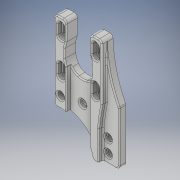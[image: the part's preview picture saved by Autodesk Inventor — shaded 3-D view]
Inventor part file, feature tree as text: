
AUTODESK INVENTOR PART (.ipt)
format: ipt  version: 2018 (Build 220112000, 112)  size: 545,792 bytes
history: native  units: in
note: dims shown in document units (in); Inventor stores cm internally (conversion verified against a paired STEP export)
features: extrude x12, sketch x12, projected_geometry x4, fillet x3, plane x2, chamfer x1
ambient origin geometry x8: Origin, YZ Plane, XZ Plane, XY Plane, X Axis, Y Axis, Z Axis, Center Point
bodies: Solid1 (feature_tree)
feature tree (34):
  extrude  "Extrusion1"  Depth=1.6929in
  extrude  "Extrusion2"  Depth=0.4331in
  fillet  "Fillet1"  Radius=1.6535in
  extrude  "Extrusion3"  Depth=1.2205in
  extrude  "Extrusion4"  Depth=0.126in
  extrude  "Extrusion5"  Depth=0.315in
  extrude  "Extrusion6"  Depth=0.2362in TaperAngle=0.0deg
  plane  "Work Plane1"
  plane  "Work Plane2"
  extrude  "Extrusion7"  Depth=0.1575in TaperAngle=0.0deg
  extrude  "Extrusion8"  Depth=0.2362in
  extrude  "Extrusion9"  Depth=0.9449in
  extrude  "Extrusion10"  Depth=0.6102in
  extrude  "Extrusion11"  Depth=1.2992in
  extrude  "Extrusion12"  Depth=0.1181in
  fillet  "Fillet2"  Radius=7.0866in
  fillet  "Fillet4"  Radius=0.2362in
  chamfer  "Chamfer1"  Distance=0.1654in
  sketch  "Sketch1"  dims[d0=3.8189in d1=1.6929in]
  sketch  "Sketch2"  dims[d2=0.4331in d3=0.4331in d4=1.6535in]
  sketch  "Sketch3"  dims[d5=0.2362in d6=0.0in d7=1.2205in]
  projected_geometry  "Projected Loop1"
  sketch  "Sketch4"  dims[d8=1.2205in d9=0.126in]
  projected_geometry  "Projected Loop2"
  sketch  "Sketch5"  dims[d10=0.2756in d11=0.315in]
  projected_geometry  "Projected Loop3"
  sketch  "Sketch6"  dims[d12=0.315in d13=0.2362in d14=0.0in]
  sketch  "Sketch8"  dims[d15=0.315in d16=0.1575in d17=0.0in]
  sketch  "Sketch9"  dims[d18=0.2362in d20=0.2362in]
  sketch  "Sketch10"  dims[d21=0.1575in d22=0.0in d23=0.9449in]
  projected_geometry  "Projected Loop4"
  sketch  "Sketch11"  dims[d24=0.315in d25=0.6102in]
  sketch  "Sketch12"  dims[d26=0.0in d27=0.0in d28=1.2992in]
  sketch  "Sketch13"  dims[d30=0.2362in d31=0.0in d32=0.1181in d33=7.0866in d34=0.2362in d35=0.0in d36=0.1654in d38=0.3937in d39=0.315in d40=0.4724in d41=0.2362in d42=0.0in d43=0.2165in d44=0.1654in d46=0.2165in d47=0.3937in d50=0.2362in d51=0.0in d52=0.2441in d53=0.0787in d54=0.0in d55=0.0787in d56=0.0in d57=0.7874in d58=0.3937in d59=0.7874in d60=0.0in d61=0.7874in d62=0.0in d63=0.1181in d65=0.0394in d66=0.0394in d67=0.0787in d68=45.0deg]
